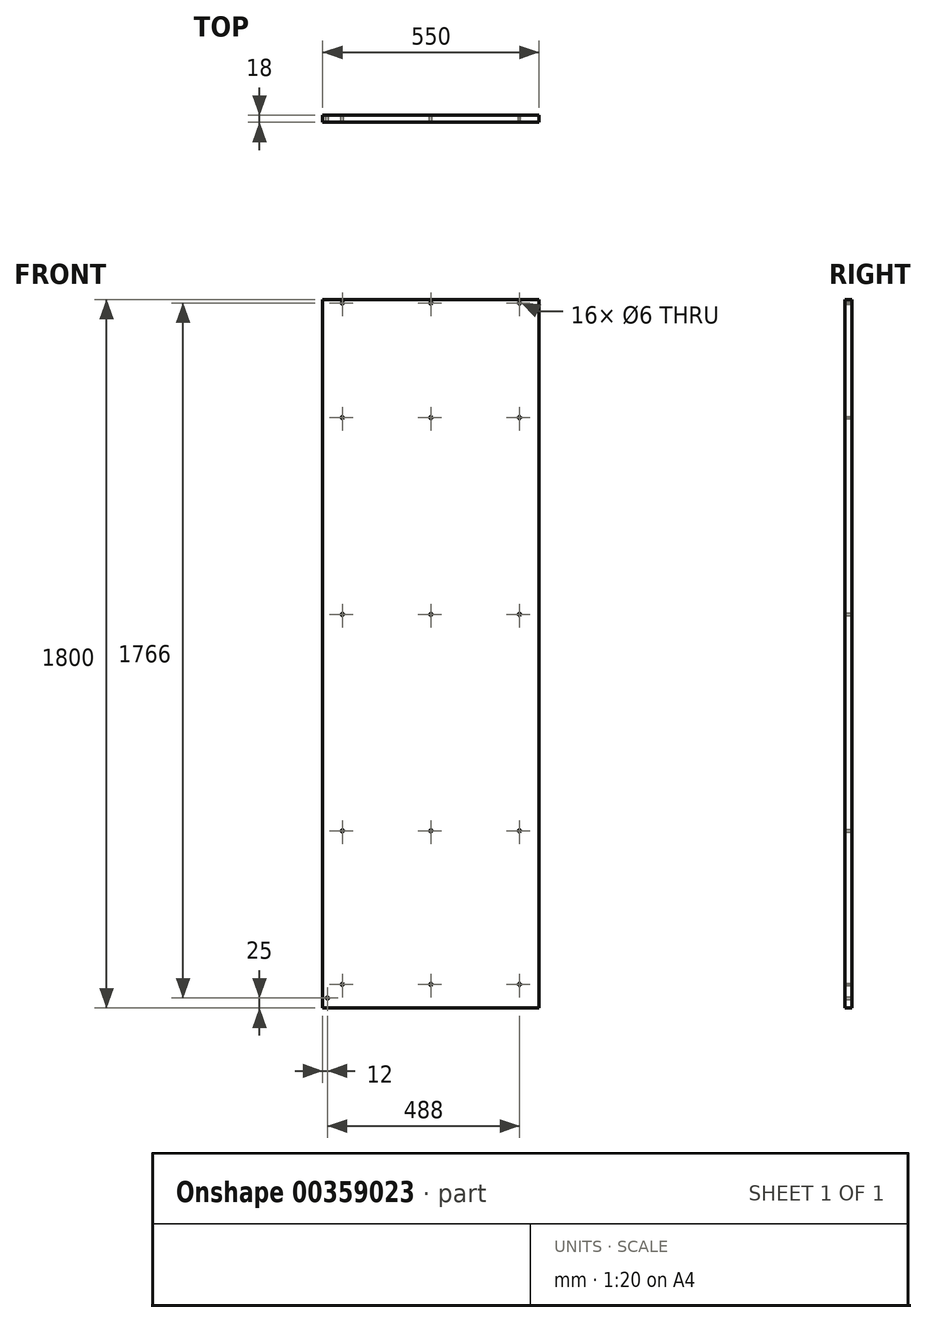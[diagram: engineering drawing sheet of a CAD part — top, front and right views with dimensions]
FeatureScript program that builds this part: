
annotation { "Feature Type Name" : "Feature", "Feature Type Description" : "" }
export const myFeature = defineFeature(function(context is Context, id is Id, definition is map)
    precondition{}
    {
        {
            var Q0;
            Q0=qCreatedBy(makeId("Front.planeOp"),FACE);
            var sketch = newSketch(context, id + "F0", { "sketchPlane" : qUnion([Q0])});
            skLineSegment(sketch, "E0.bottom", {"start": v(0, 0) * mm, "end": v(550, 0) * mm});
            skLineSegment(sketch, "E0.top", {"start": v(0, 1800) * mm, "end": v(550, 1800) * mm});
            skLineSegment(sketch, "E0.left", {"start": v(0, 0) * mm, "end": v(0, 1800) * mm});
            skLineSegment(sketch, "E0.right", {"start": v(550, 0) * mm, "end": v(550, 1800) * mm});
            skLineSegment(sketch, "E1", {"start": v(-125.66, 1791) * mm, "end": v(692.83, 1791) * mm, "construction": true});
            skLineSegment(sketch, "E2", {"start": v(-137.4, 1000) * mm, "end": v(713.36, 1000) * mm, "construction": true});
            skLineSegment(sketch, "E3", {"start": v(-125.66, 1500) * mm, "end": v(713.36, 1500) * mm, "construction": true});
            skLineSegment(sketch, "E4", {"start": v(-204.39, 60) * mm, "end": v(713.36, 60) * mm, "construction": true});
            skLineSegment(sketch, "E5", {"start": v(-169.85, 450) * mm, "end": v(713.36, 450) * mm, "construction": true});
            skLineSegment(sketch, "E6", {"start": v(50, 2111.2) * mm, "end": v(50, -499.74) * mm, "construction": true});
            skLineSegment(sketch, "E7", {"start": v(275, 2158.14) * mm, "end": v(275, -441.07) * mm, "construction": true});
            skPoint(sketch, "E7.startSnap0", {"position": v(275, 0) * mm});
            skLineSegment(sketch, "E8", {"start": v(500, 2128.8) * mm, "end": v(500, -441.07) * mm, "construction": true});
            skCircle(sketch, "E9", {"center": v(500, 1791) * mm, "radius": 3 * mm});
            skCircle(sketch, "E10", {"center": v(275, 1791) * mm, "radius": 3 * mm});
            skCircle(sketch, "E11", {"center": v(50, 1791) * mm, "radius": 3 * mm});
            skCircle(sketch, "E12", {"center": v(50, 1500) * mm, "radius": 3 * mm});
            skCircle(sketch, "E13", {"center": v(275, 1500) * mm, "radius": 3 * mm});
            skCircle(sketch, "E14", {"center": v(500, 1500) * mm, "radius": 3 * mm});
            skCircle(sketch, "E15", {"center": v(50, 1000) * mm, "radius": 3 * mm});
            skCircle(sketch, "E16", {"center": v(275, 1000) * mm, "radius": 3 * mm});
            skCircle(sketch, "E17", {"center": v(500, 1000) * mm, "radius": 3 * mm});
            skCircle(sketch, "E18", {"center": v(50, 450) * mm, "radius": 3 * mm});
            skCircle(sketch, "E19", {"center": v(275, 450) * mm, "radius": 3 * mm});
            skCircle(sketch, "E20", {"center": v(500, 450) * mm, "radius": 3 * mm});
            skCircle(sketch, "E21", {"center": v(50, 60) * mm, "radius": 3 * mm});
            skCircle(sketch, "E22", {"center": v(275, 60) * mm, "radius": 3 * mm});
            skCircle(sketch, "E23", {"center": v(500, 60) * mm, "radius": 3 * mm});
            skLineSegment(sketch, "E24", {"start": v(-94.42, 25) * mm, "end": v(650.33, 25) * mm, "construction": true});
            skCircle(sketch, "E25", {"center": v(12, 25) * mm, "radius": 3 * mm});
            skSolve(sketch);
        }
        {
            var Q0;
            Q0 = qSketchRegion(id + "F0", true);
            extrude(context, id + "F1", {"entities" : qUnion([Q0]), "depth" : 18 * mm});
        }
    });
